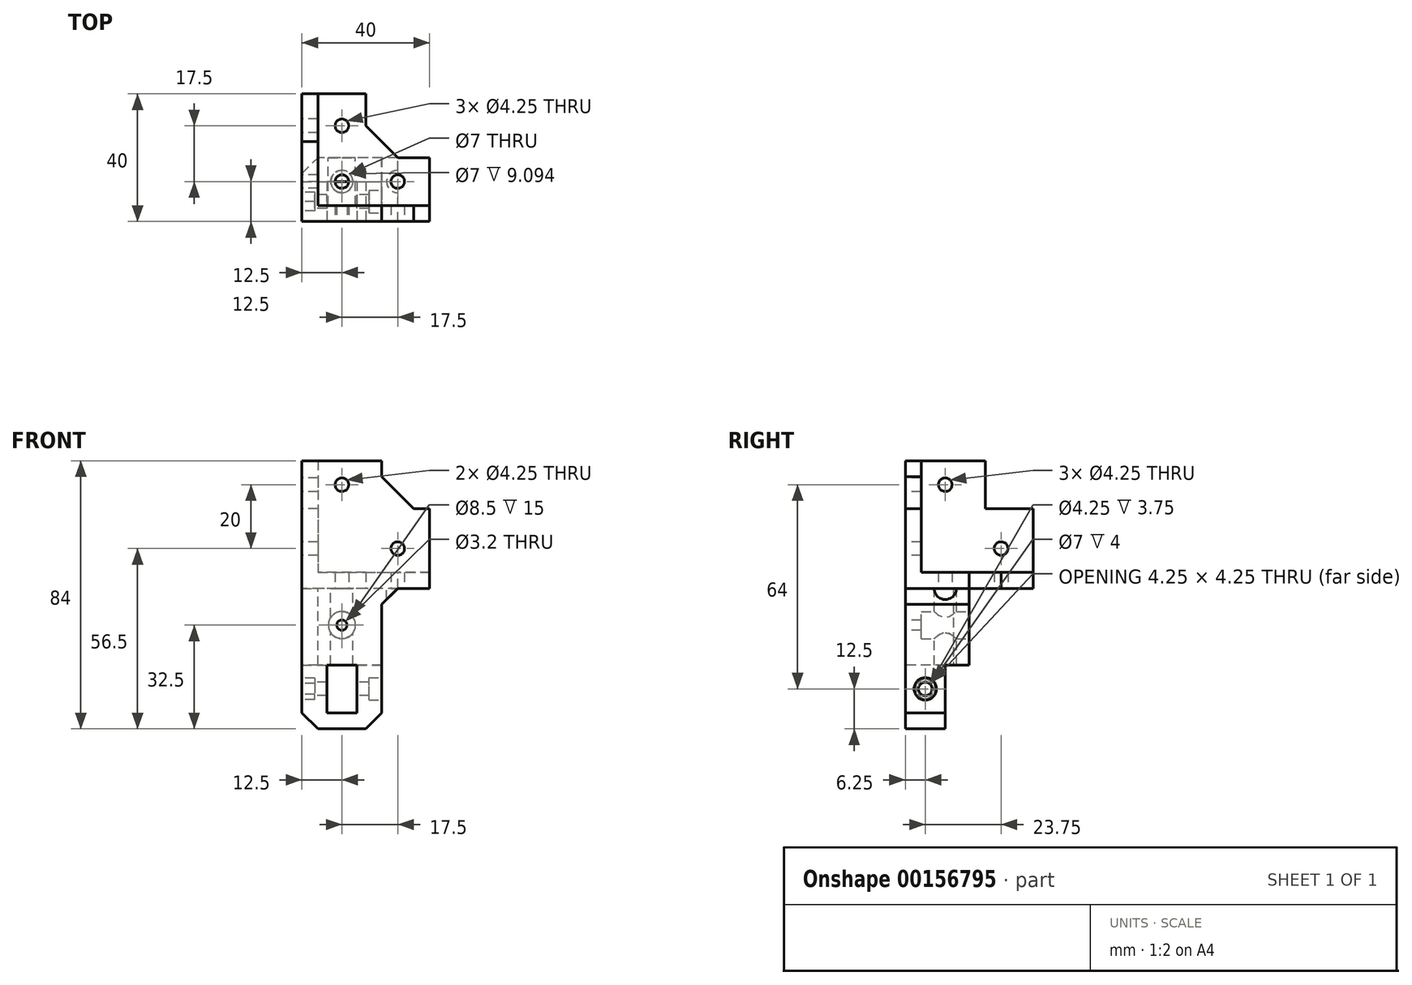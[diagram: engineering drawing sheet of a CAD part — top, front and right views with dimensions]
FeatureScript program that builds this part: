
annotation { "Feature Type Name" : "Feature", "Feature Type Description" : "" }
export const myFeature = defineFeature(function(context is Context, id is Id, definition is map)
    precondition{}
    {
        {
            var Q0;
            Q0=qCreatedBy(makeId("Top.planeOp"),FACE);
            var sketch = newSketch(context, id + "F0", { "sketchPlane" : qUnion([Q0])});
            skLineSegment(sketch, "E0", {"start": v(0, 40) * mm, "end": v(-20, 40) * mm});
            skLineSegment(sketch, "E1", {"start": v(-20, 40) * mm, "end": v(-20, 0) * mm});
            skLineSegment(sketch, "E2", {"start": v(-20, 0) * mm, "end": v(20, 0) * mm});
            skLineSegment(sketch, "E3", {"start": v(20, 0) * mm, "end": v(20, 20) * mm});
            skLineSegment(sketch, "E4", {"start": v(20, 20) * mm, "end": v(0, 20) * mm});
            skLineSegment(sketch, "E5", {"start": v(0, 20) * mm, "end": v(0, 40) * mm});
            skCircle(sketch, "E6", {"center": v(-7.5, 30) * mm, "radius": 2.12 * mm});
            skCircle(sketch, "E7", {"center": v(10, 12.5) * mm, "radius": 2.12 * mm});
            skCircle(sketch, "E8", {"center": v(-7.5, 12.5) * mm, "radius": 2.12 * mm});
            skSolve(sketch);
        }
        {
            var Q0;
            Q0=qSketchRegion(id+"F0",true);
            extrude(context, id + "F1", {"entities" : qUnion([Q0]), "depth" : 5 * mm});
        }
        {
            var Q0;
            Q0=makeQuery(id+"F1.opExtrude","CAP_FACE",FACE,{"disambiguationData":[OSD([sQuery(id+"F0.wireOp",EDGE,"E0"),sQuery(id+"F0.wireOp",EDGE,"E1"),sQuery(id+"F0.wireOp",EDGE,"E2"),sQuery(id+"F0.wireOp",EDGE,"E3"),sQuery(id+"F0.wireOp",EDGE,"E4"),sQuery(id+"F0.wireOp",EDGE,"E5"),sQuery(id+"F0.wireOp",EDGE,"E6"),sQuery(id+"F0.wireOp",EDGE,"E7")])],"isStart":false});
            var sketch = newSketch(context, id + "F2", { "sketchPlane" : qUnion([Q0])});
            skLineSegment(sketch, "E9", {"start": v(-20, 40) * mm, "end": v(-15, 40) * mm});
            skLineSegment(sketch, "E10", {"start": v(-15, 40) * mm, "end": v(-15, 5) * mm});
            skLineSegment(sketch, "E11", {"start": v(-15, 5) * mm, "end": v(20, 5) * mm});
            skLineSegment(sketch, "E12", {"start": v(20, 5) * mm, "end": v(20, 0) * mm});
            skLineSegment(sketch, "E13", {"start": v(20, 0) * mm, "end": v(-20, 0) * mm});
            skLineSegment(sketch, "E14", {"start": v(-20, 0) * mm, "end": v(-20, 40) * mm});
            skSolve(sketch);
        }
        {
            var Q0;
            Q0=qSketchRegion(id+"F2",true);
            extrude(context, id + "F3", {"entities" : qUnion([Q0]), "operationType" : NewBodyOperationType.ADD, "depth" : 20 * mm});
        }
        {
            var Q0;
            Q0=makeQuery(id+"F3.opExtrude","CAP_FACE",FACE,{"disambiguationData":[OSD([sQuery(id+"F2.wireOp",EDGE,"E9"),sQuery(id+"F2.wireOp",EDGE,"E10"),sQuery(id+"F2.wireOp",EDGE,"E11"),sQuery(id+"F2.wireOp",EDGE,"E12"),sQuery(id+"F2.wireOp",EDGE,"E13"),sQuery(id+"F2.wireOp",EDGE,"E14")])],"isStart":false});
            var sketch = newSketch(context, id + "F4", { "sketchPlane" : qUnion([Q0])});
            skLineSegment(sketch, "E15", {"start": v(-15, 25) * mm, "end": v(-20, 25) * mm});
            skLineSegment(sketch, "E16", {"start": v(-20, 25) * mm, "end": v(-20, 0) * mm});
            skLineSegment(sketch, "E17", {"start": v(-20, 0) * mm, "end": v(5, 0) * mm});
            skLineSegment(sketch, "E18", {"start": v(5, 0) * mm, "end": v(5, 5) * mm});
            skLineSegment(sketch, "E19", {"start": v(5, 5) * mm, "end": v(-15, 5) * mm});
            skLineSegment(sketch, "E20", {"start": v(-15, 5) * mm, "end": v(-15, 25) * mm});
            skSolve(sketch);
        }
        {
            var Q0;
            Q0=qSketchRegion(id+"F4",true);
            extrude(context, id + "F5", {"entities" : qUnion([Q0]), "operationType" : NewBodyOperationType.ADD, "depth" : 15 * mm});
        }
        {
            var Q0;
            Q0=makeQuery(id+"F1.opExtrude","SWEPT_EDGE",EDGE,{"disambiguationData":[OSD([sQuery(id+"F0.wireOp",EDGE,"E4"),sQuery(id+"F0.wireOp",EDGE,"E5")])]});
            var Q1;
            Q1=makeQuery(id+"F5.opExtrude","CAP_EDGE",EDGE,{"disambiguationData":[OSD([sQuery(id+"F4.wireOp",EDGE,"E15")])],"isStart":true});
            var Q2;
            Q2=makeQuery(id+"F5.opExtrude","CAP_EDGE",EDGE,{"disambiguationData":[OSD([sQuery(id+"F4.wireOp",EDGE,"E18")])],"isStart":true});
            chamfer(context, id + "F6", {"entities" : qUnion([Q0, Q1, Q2]), "width" : 10 * mm, "tangentPropagation" : true});
        }
        {
            var Q0;
            Q0=makeQuery(id+"F5.boolean.opBoolean","MERGE",FACE,{"derivedFrom":[makeQuery(id+"F3.boolean.opBoolean","MERGE",FACE,{"derivedFrom":[makeQuery(id+"F1.opExtrude","SWEPT_FACE",FACE,{"disambiguationData":[OSD([sQuery(id+"F0.wireOp",EDGE,"E2")])]}),makeQuery(id+"F3.opExtrude","SWEPT_FACE",FACE,{"disambiguationData":[OSD([sQuery(id+"F2.wireOp",EDGE,"E13")])]})]}),makeQuery(id+"F5.opExtrude","SWEPT_FACE",FACE,{"disambiguationData":[OSD([sQuery(id+"F4.wireOp",EDGE,"E17")])]})]});
            var sketch = newSketch(context, id + "F7", { "sketchPlane" : qUnion([Q0])});
            skCircle(sketch, "E21", {"center": v(-7.5, 32.5) * mm, "radius": 2.12 * mm});
            skCircle(sketch, "E22", {"center": v(10, 12.5) * mm, "radius": 2.12 * mm});
            skSolve(sketch);
        }
        {
            var Q0;
            Q0=qSketchRegion(id+"F7",true);
            extrude(context, id + "F8", {"entities" : qUnion([Q0]), "operationType" : NewBodyOperationType.REMOVE, "oppositeDirection" : true, "depth" : 5 * mm});
        }
        {
            var Q0;
            Q0=makeQuery(id+"F5.boolean.opBoolean","MERGE",FACE,{"derivedFrom":[makeQuery(id+"F3.boolean.opBoolean","MERGE",FACE,{"derivedFrom":[makeQuery(id+"F1.opExtrude","SWEPT_FACE",FACE,{"disambiguationData":[OSD([sQuery(id+"F0.wireOp",EDGE,"E1")])]}),makeQuery(id+"F3.opExtrude","SWEPT_FACE",FACE,{"disambiguationData":[OSD([sQuery(id+"F2.wireOp",EDGE,"E14")])]})]}),makeQuery(id+"F5.opExtrude","SWEPT_FACE",FACE,{"disambiguationData":[OSD([sQuery(id+"F4.wireOp",EDGE,"E16")])]})]});
            var sketch = newSketch(context, id + "F9", { "sketchPlane" : qUnion([Q0])});
            skCircle(sketch, "E23", {"center": v(-12.5, 32.5) * mm, "radius": 2.12 * mm});
            skCircle(sketch, "E24", {"center": v(-30, 12.5) * mm, "radius": 2.12 * mm});
            skSolve(sketch);
        }
        {
            var Q0;
            Q0=qSketchRegion(id+"F9",true);
            extrude(context, id + "F10", {"entities" : qUnion([Q0]), "operationType" : NewBodyOperationType.REMOVE, "oppositeDirection" : true, "depth" : 5 * mm});
        }
        {
            var Q0;
            Q0=makeQuery(id+"F1.opExtrude","CAP_FACE",FACE,{"disambiguationData":[OSD([sQuery(id+"F0.wireOp",EDGE,"E0"),sQuery(id+"F0.wireOp",EDGE,"E1"),sQuery(id+"F0.wireOp",EDGE,"E2"),sQuery(id+"F0.wireOp",EDGE,"E3"),sQuery(id+"F0.wireOp",EDGE,"E4"),sQuery(id+"F0.wireOp",EDGE,"E5"),sQuery(id+"F0.wireOp",EDGE,"E6"),sQuery(id+"F0.wireOp",EDGE,"E7"),sQuery(id+"F0.wireOp",EDGE,"E8")])],"isStart":true});
            var sketch = newSketch(context, id + "F11", { "sketchPlane" : qUnion([Q0])});
            skLineSegment(sketch, "E25.bottom", {"start": v(20, -20) * mm, "end": v(-20, -20) * mm});
            skLineSegment(sketch, "E25.top", {"start": v(20, 0) * mm, "end": v(-20, 0) * mm});
            skLineSegment(sketch, "E25.left", {"start": v(20, -20) * mm, "end": v(20, 0) * mm});
            skLineSegment(sketch, "E25.right", {"start": v(-20, -20) * mm, "end": v(-20, 0) * mm});
            skPoint(sketch, "E25.middle", {"position": v(0, -10) * mm});
            skPoint(sketch, "E26.visualSharp", {"position": v(-20, 0) * mm});
            skLineSegment(sketch, "E26.filletArc", {"start": v(-20, 0) * mm, "end": v(-20, 0) * mm});
            skCircle(sketch, "E27", {"center": v(10, -12.5) * mm, "radius": 2.12 * mm});
            skCircle(sketch, "E28", {"center": v(-7.5, -12.5) * mm, "radius": 2.12 * mm});
            skSolve(sketch);
        }
        {
            var Q0;
            Q0=qSketchRegion(id+"F11",true);
            extrude(context, id + "F12", {"entities" : qUnion([Q0]), "operationType" : NewBodyOperationType.ADD, "depth" : 24 * mm});
        }
        {
            var Q0;
            Q0=makeQuery(id+"F12.boolean.opBoolean","MERGE",FACE,{"derivedFrom":[makeQuery(id+"F1.opExtrude","SWEPT_FACE",FACE,{"disambiguationData":[OSD([sQuery(id+"F0.wireOp",EDGE,"E4")])]}),makeQuery(id+"F12.opExtrude","SWEPT_FACE",FACE,{"disambiguationData":[OSD([sQuery(id+"F11.wireOp",EDGE,"E25.bottom")])]})]});
            var sketch = newSketch(context, id + "F13", { "sketchPlane" : qUnion([Q0])});
            skLineSegment(sketch, "E29", {"start": v(20, -11.5) * mm, "end": v(20, -24) * mm});
            skLineSegment(sketch, "E30", {"start": v(20, -24) * mm, "end": v(7.5, -24) * mm});
            skPoint(sketch, "E31.orphan", {"position": v(7.5, -24) * mm});
            skCircle(sketch, "E32", {"center": v(7.5, -11.5) * mm, "radius": 4.25 * mm});
            skLineSegment(sketch, "E33", {"start": v(-5, -11.5) * mm, "end": v(-5, 0) * mm});
            skLineSegment(sketch, "E34", {"start": v(-5, 0) * mm, "end": v(-20, 0) * mm});
            skLineSegment(sketch, "E35", {"start": v(-20, 0) * mm, "end": v(-20, -24) * mm});
            skLineSegment(sketch, "E36", {"start": v(-20, -24) * mm, "end": v(7.5, -24) * mm});
            skLineSegment(sketch, "E37", {"start": v(-5, -11.5) * mm, "end": v(-5, -24) * mm});
            skSolve(sketch);
        }
        {
            var Q0;
            Q0=qSketchRegion(id+"F13",true);
            extrude(context, id + "F14", {"entities" : qUnion([Q0]), "operationType" : NewBodyOperationType.REMOVE, "oppositeDirection" : true, "depth" : 25 * mm});
        }
        {
            var Q0;
            Q0=makeQuery(id+"F14.boolean.opBoolean","MERGE",FACE,{"derivedFrom":[makeQuery(id+"F1.opExtrude","CAP_FACE",FACE,{"disambiguationData":[OSD([sQuery(id+"F0.wireOp",EDGE,"E0"),sQuery(id+"F0.wireOp",EDGE,"E1"),sQuery(id+"F0.wireOp",EDGE,"E2"),sQuery(id+"F0.wireOp",EDGE,"E3"),sQuery(id+"F0.wireOp",EDGE,"E4"),sQuery(id+"F0.wireOp",EDGE,"E5"),sQuery(id+"F0.wireOp",EDGE,"E6"),sQuery(id+"F0.wireOp",EDGE,"E7"),sQuery(id+"F0.wireOp",EDGE,"E8")])],"isStart":true}),makeQuery(id+"F14.opExtrude","SWEPT_FACE",FACE,{"disambiguationData":[OSD([sQuery(id+"F13.wireOp",EDGE,"E34")])]})]});
            var sketch = newSketch(context, id + "F15", { "sketchPlane" : qUnion([Q0])});
            skCircle(sketch, "E38", {"center": v(-7.5, -12.5) * mm, "radius": 3.5 * mm});
            skSolve(sketch);
        }
        {
            var Q0;
            Q0=qSketchRegion(id+"F15",true);
            extrude(context, id + "F16", {"entities" : qUnion([Q0]), "operationType" : NewBodyOperationType.REMOVE, "depth" : 25 * mm});
        }
        {
            var Q0;
            Q0=makeQuery(id+"F12.boolean.opBoolean","MERGE",FACE,{"derivedFrom":[makeQuery(id+"F5.boolean.opBoolean","MERGE",FACE,{"derivedFrom":[makeQuery(id+"F3.boolean.opBoolean","MERGE",FACE,{"derivedFrom":[makeQuery(id+"F1.opExtrude","SWEPT_FACE",FACE,{"disambiguationData":[OSD([sQuery(id+"F0.wireOp",EDGE,"E2")])]}),makeQuery(id+"F3.opExtrude","SWEPT_FACE",FACE,{"disambiguationData":[OSD([sQuery(id+"F2.wireOp",EDGE,"E13")])]})]}),makeQuery(id+"F5.opExtrude","SWEPT_FACE",FACE,{"disambiguationData":[OSD([sQuery(id+"F4.wireOp",EDGE,"E17")])]})]}),makeQuery(id+"F12.opExtrude","SWEPT_FACE",FACE,{"disambiguationData":[OSD([sQuery(id+"F11.wireOp",EDGE,"E25.top")])]})]});
            var sketch = newSketch(context, id + "F17", { "sketchPlane" : qUnion([Q0])});
            skCircle(sketch, "E39", {"center": v(-7.5, -11.5) * mm, "radius": 4.25 * mm});
            skCircle(sketch, "E40", {"center": v(-7.5, -11.5) * mm, "radius": 1.6 * mm});
            skSolve(sketch);
        }
        {
            var Q0;
            Q0=qSketchRegion(id+"F17",true);
            extrude(context, id + "F18", {"entities" : qUnion([Q0]), "operationType" : NewBodyOperationType.ADD, "oppositeDirection" : true, "depth" : 5 * mm});
        }
        {
            var Q0;
            Q0=makeQuery(id+"FNQfyr8qSEigWVF_1.boolean.opBoolean","MERGE",EDGE,{"derivedFrom":[makeQuery(id+"F14.boolean.opBoolean","COPY",EDGE,{"derivedFrom":makeQuery(id+"F14.opExtrude","SWEPT_EDGE",EDGE,{"disambiguationData":[OSD([sQuery(id+"F11.wireOp",EDGE,"E25.bottom"),sQuery(id+"F13.wireOp",EDGE,"E33"),sQuery(id+"F13.wireOp",EDGE,"E34")])]})}),makeQuery(id+"FNQfyr8qSEigWVF_1.opExtrude","SWEPT_EDGE",EDGE,{"disambiguationData":[OSD([sQuery(id+"F1wlyD548anW5wl_1.wireOp",EDGE,"YZkgPk9V-HXlL-QKvk-AvvO-C27N44Z9oYY3.bottom"),sQuery(id+"F1wlyD548anW5wl_1.wireOp",EDGE,"YZkgPk9V-HXlL-QKvk-AvvO-C27N44Z9oYY3.left")])]})]});
            chamfer(context, id + "F19", {"entities" : qUnion([Q0]), "width" : 5 * mm, "tangentPropagation" : true});
        }
        {
            var Q0;
            Q0=makeQuery(id+"F18.boolean.opBoolean","MERGE",FACE,{"derivedFrom":[makeQuery(id+"F12.boolean.opBoolean","MERGE",FACE,{"derivedFrom":[makeQuery(id+"F5.boolean.opBoolean","MERGE",FACE,{"derivedFrom":[makeQuery(id+"F3.boolean.opBoolean","MERGE",FACE,{"derivedFrom":[makeQuery(id+"F1.opExtrude","SWEPT_FACE",FACE,{"disambiguationData":[OSD([sQuery(id+"F0.wireOp",EDGE,"E2")])]}),makeQuery(id+"F3.opExtrude","SWEPT_FACE",FACE,{"disambiguationData":[OSD([sQuery(id+"F2.wireOp",EDGE,"E13")])]})]}),makeQuery(id+"F5.opExtrude","SWEPT_FACE",FACE,{"disambiguationData":[OSD([sQuery(id+"F4.wireOp",EDGE,"E17")])]})]}),makeQuery(id+"F12.opExtrude","SWEPT_FACE",FACE,{"disambiguationData":[OSD([sQuery(id+"F11.wireOp",EDGE,"E25.top")])]})]}),makeQuery(id+"F18.opExtrude","CAP_FACE",FACE,{"disambiguationData":[OSD([sQuery(id+"F17.wireOp",EDGE,"E39"),sQuery(id+"F17.wireOp",EDGE,"E40")])],"isStart":true})]});
            var sketch = newSketch(context, id + "F20", { "sketchPlane" : qUnion([Q0])});
            skLineSegment(sketch, "E41", {"start": v(-20, -24) * mm, "end": v(-20, -44) * mm});
            skLineSegment(sketch, "E42", {"start": v(-20, -44) * mm, "end": v(5, -44) * mm});
            skLineSegment(sketch, "E43", {"start": v(5, -44) * mm, "end": v(5, -24) * mm});
            skLineSegment(sketch, "E44", {"start": v(5, -24) * mm, "end": v(-2.75, -24) * mm});
            skLineSegment(sketch, "E45", {"start": v(-2.75, -24) * mm, "end": v(-2.75, -39) * mm});
            skLineSegment(sketch, "E46", {"start": v(-2.75, -39) * mm, "end": v(-12.25, -39) * mm});
            skLineSegment(sketch, "E47", {"start": v(-12.25, -39) * mm, "end": v(-12.25, -24) * mm});
            skLineSegment(sketch, "E48", {"start": v(-12.25, -24) * mm, "end": v(-20, -24) * mm});
            skSolve(sketch);
        }
        {
            var Q0;
            Q0=qSketchRegion(id+"F20",true);
            extrude(context, id + "F21", {"entities" : qUnion([Q0]), "operationType" : NewBodyOperationType.ADD, "oppositeDirection" : true, "depth" : 12.5 * mm});
        }
        {
            var Q0;
            Q0=makeQuery(id+"F21.opExtrude","SWEPT_EDGE",EDGE,{"disambiguationData":[OSD([sQuery(id+"F20.wireOp",EDGE,"E41"),sQuery(id+"F20.wireOp",EDGE,"E42")])]});
            var Q1;
            Q1=makeQuery(id+"F21.opExtrude","SWEPT_EDGE",EDGE,{"disambiguationData":[OSD([sQuery(id+"F20.wireOp",EDGE,"E42"),sQuery(id+"F20.wireOp",EDGE,"E43")])]});
            var Q2;
            Q2=makeQuery(id+"F14.boolean.opBoolean","COPY",EDGE,{"derivedFrom":makeQuery(id+"F14.opExtrude","CAP_EDGE",EDGE,{"disambiguationData":[OSD([sQuery(id+"F13.wireOp",EDGE,"E33"),sQuery(id+"F13.wireOp",EDGE,"E37")])],"isStart":true})});
            var Q3;
            Q3=makeQuery(id+"F12.opExtrude","SWEPT_EDGE",EDGE,{"disambiguationData":[OSD([sQuery(id+"F0.wireOp",EDGE,"E1"),sQuery(id+"F11.wireOp",EDGE,"E25.bottom"),sQuery(id+"F11.wireOp",EDGE,"E25.right")])]});
            chamfer(context, id + "F22", {"entities" : qUnion([Q0, Q1, Q2, Q3]), "width" : 5 * mm, "tangentPropagation" : true});
        }
        {
            var Q0;
            Q0=makeQuery(id+"F19.opChamfer","SPLIT",FACE,{"disambiguationData":[OD(1.0)],"derivedFrom":makeQuery(id+"F14.boolean.opBoolean","MERGE",FACE,{"derivedFrom":[makeQuery(id+"F1.opExtrude","CAP_FACE",FACE,{"disambiguationData":[OSD([sQuery(id+"F0.wireOp",EDGE,"E0"),sQuery(id+"F0.wireOp",EDGE,"E1"),sQuery(id+"F0.wireOp",EDGE,"E2"),sQuery(id+"F0.wireOp",EDGE,"E3"),sQuery(id+"F0.wireOp",EDGE,"E4"),sQuery(id+"F0.wireOp",EDGE,"E5"),sQuery(id+"F0.wireOp",EDGE,"E6"),sQuery(id+"F0.wireOp",EDGE,"E7"),sQuery(id+"F0.wireOp",EDGE,"E8")])],"isStart":true}),makeQuery(id+"F14.opExtrude","SWEPT_FACE",FACE,{"disambiguationData":[OSD([sQuery(id+"F13.wireOp",EDGE,"E34")])]})]})});
            var sketch = newSketch(context, id + "F23", { "sketchPlane" : qUnion([Q0])});
            skCircle(sketch, "E49", {"center": v(10, -12.5) * mm, "radius": 3.5 * mm});
            skSolve(sketch);
        }
        {
            var Q0;
            Q0=qSketchRegion(id+"F23",true);
            extrude(context, id + "F24", {"entities" : qUnion([Q0]), "operationType" : NewBodyOperationType.REMOVE, "endBound" : BoundingType.THROUGH_ALL, "depth" : 25 * mm});
        }
        {
            var Q0;
            Q0=makeQuery(id+"F21.boolean.opBoolean","MERGE",FACE,{"derivedFrom":[makeQuery(id+"F12.boolean.opBoolean","MERGE",FACE,{"derivedFrom":[makeQuery(id+"F5.boolean.opBoolean","MERGE",FACE,{"derivedFrom":[makeQuery(id+"F3.boolean.opBoolean","MERGE",FACE,{"derivedFrom":[makeQuery(id+"F1.opExtrude","SWEPT_FACE",FACE,{"disambiguationData":[OSD([sQuery(id+"F0.wireOp",EDGE,"E1")])]}),makeQuery(id+"F3.opExtrude","SWEPT_FACE",FACE,{"disambiguationData":[OSD([sQuery(id+"F2.wireOp",EDGE,"E14")])]})]}),makeQuery(id+"F5.opExtrude","SWEPT_FACE",FACE,{"disambiguationData":[OSD([sQuery(id+"F4.wireOp",EDGE,"E16")])]})]}),makeQuery(id+"F12.opExtrude","SWEPT_FACE",FACE,{"disambiguationData":[OSD([sQuery(id+"F11.wireOp",EDGE,"E25.right")])]})]}),makeQuery(id+"F21.opExtrude","SWEPT_FACE",FACE,{"disambiguationData":[OSD([sQuery(id+"F20.wireOp",EDGE,"E41")])]})]});
            var sketch = newSketch(context, id + "F25", { "sketchPlane" : qUnion([Q0])});
            skCircle(sketch, "E50", {"center": v(-6.25, -31.5) * mm, "radius": 2.12 * mm});
            skSolve(sketch);
        }
        {
            var Q0;
            Q0=qSketchRegion(id+"F25",true);
            extrude(context, id + "F26", {"entities" : qUnion([Q0]), "operationType" : NewBodyOperationType.REMOVE, "endBound" : BoundingType.THROUGH_ALL, "oppositeDirection" : true, "depth" : 25 * mm});
        }
        {
            var Q0;
            Q0=makeQuery(id+"F21.boolean.opBoolean","MERGE",FACE,{"derivedFrom":[makeQuery(id+"F12.boolean.opBoolean","MERGE",FACE,{"derivedFrom":[makeQuery(id+"F5.boolean.opBoolean","MERGE",FACE,{"derivedFrom":[makeQuery(id+"F3.boolean.opBoolean","MERGE",FACE,{"derivedFrom":[makeQuery(id+"F1.opExtrude","SWEPT_FACE",FACE,{"disambiguationData":[OSD([sQuery(id+"F0.wireOp",EDGE,"E1")])]}),makeQuery(id+"F3.opExtrude","SWEPT_FACE",FACE,{"disambiguationData":[OSD([sQuery(id+"F2.wireOp",EDGE,"E14")])]})]}),makeQuery(id+"F5.opExtrude","SWEPT_FACE",FACE,{"disambiguationData":[OSD([sQuery(id+"F4.wireOp",EDGE,"E16")])]})]}),makeQuery(id+"F12.opExtrude","SWEPT_FACE",FACE,{"disambiguationData":[OSD([sQuery(id+"F11.wireOp",EDGE,"E25.right")])]})]}),makeQuery(id+"F21.opExtrude","SWEPT_FACE",FACE,{"disambiguationData":[OSD([sQuery(id+"F20.wireOp",EDGE,"E41")])]})]});
            var sketch = newSketch(context, id + "F27", { "sketchPlane" : qUnion([Q0])});
            skCircle(sketch, "E51.cCircle", {"center": v(-6.25, -31.5) * mm, "radius": 2.93 * mm, "construction": true});
            skLineSegment(sketch, "E51.0", {"start": v(-3.33, -29.81) * mm, "end": v(-3.33, -33.19) * mm});
            skLineSegment(sketch, "E51.1", {"start": v(-3.33, -33.19) * mm, "end": v(-6.25, -34.88) * mm});
            skLineSegment(sketch, "E51.2", {"start": v(-6.25, -34.88) * mm, "end": v(-9.17, -33.19) * mm});
            skLineSegment(sketch, "E51.3", {"start": v(-9.18, -33.19) * mm, "end": v(-9.18, -29.81) * mm});
            skLineSegment(sketch, "E51.4", {"start": v(-9.17, -29.81) * mm, "end": v(-6.25, -28.12) * mm});
            skLineSegment(sketch, "E51.5", {"start": v(-6.25, -28.12) * mm, "end": v(-3.33, -29.81) * mm});
            skPoint(sketch, "E51.0.midPoint", {"position": v(-3.33, -31.5) * mm});
            skSolve(sketch);
        }
        {
            var Q0;
            Q0=qSketchRegion(id+"F27",true);
            extrude(context, id + "F28", {"entities" : qUnion([Q0]), "operationType" : NewBodyOperationType.REMOVE, "oppositeDirection" : true, "depth" : 4 * mm});
        }
        {
            var Q0;
            Q0=makeQuery(id+"F21.boolean.opBoolean","MERGE",FACE,{"derivedFrom":[makeQuery(id+"F14.boolean.opBoolean","COPY",FACE,{"derivedFrom":makeQuery(id+"F14.opExtrude","SWEPT_FACE",FACE,{"disambiguationData":[OSD([sQuery(id+"F13.wireOp",EDGE,"E33"),sQuery(id+"F13.wireOp",EDGE,"E37")])]})}),makeQuery(id+"F21.opExtrude","SWEPT_FACE",FACE,{"disambiguationData":[OSD([sQuery(id+"F20.wireOp",EDGE,"E43")])]})]});
            var sketch = newSketch(context, id + "F29", { "sketchPlane" : qUnion([Q0])});
            skCircle(sketch, "E52", {"center": v(6.25, -31.5) * mm, "radius": 3.5 * mm});
            skSolve(sketch);
        }
        {
            var Q0;
            Q0=qSketchRegion(id+"F29",true);
            extrude(context, id + "F30", {"entities" : qUnion([Q0]), "operationType" : NewBodyOperationType.REMOVE, "oppositeDirection" : true, "depth" : 4 * mm});
        }
    });
